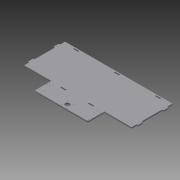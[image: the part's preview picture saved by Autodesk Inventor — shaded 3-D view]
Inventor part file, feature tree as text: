
AUTODESK INVENTOR PART (.ipt)
format: ipt  version: 2013 (Build 170138000, 138)  size: 482,304 bytes
history: native  units: mm
features: reference x12, extrude x10, sketch x10, fillet x1, mirror x1
ambient origin geometry x8: Origin, YZ Plane, XZ Plane, XY Plane, X Axis, Y Axis, Z Axis, Center Point
bodies: Solid1 (feature_tree)
feature tree (34):
  extrude  "Extrusion1"  Depth=81.477mm
  fillet  "Fillet1"  Radius=525.0mm
  extrude  "Extrusion2"  Depth=6.477mm TaperAngle=0.0deg
  extrude  "Extrusion3"  Depth=10.0mm TaperAngle=0.0deg
  extrude  "Extrusion4"  Depth=42.0mm
  extrude  "Extrusion5"  Depth=31.0mm
  mirror  "Mirror2"
  extrude  "Extrusion6"  Depth=10.0mm TaperAngle=0.0deg
  extrude  "Extrusion7"  Depth=25.0mm
  extrude  "Extrusion8"  Depth=6.477mm
  extrude  "Extrusion9"  Depth=2.5mm
  extrude  "Extrusion10"  Depth=1.5mm
  sketch  "Sketch1"  dims[d0=260.0mm d2=81.477mm d3=525.0mm]
  sketch  "Sketch2"  dims[d4=200.0mm d5=6.477mm d6=0.0mm]
  reference  "Reference1"
  reference  "Reference2"
  sketch  "Sketch3"  dims[d7=5.0mm d8=10.0mm d9=0.0mm]
  sketch  "Sketch4"  dims[d10=9.5mm d11=42.0mm]
  sketch  "Sketch5"  dims[d12=22.0mm d13=31.0mm]
  sketch  "Sketch6"  dims[d14=3.0mm d15=10.0mm d16=0.0mm]
  reference  "Reference3"
  reference  "Reference4"
  reference  "Reference5"
  reference  "Reference6"
  reference  "Reference7"
  reference  "Reference8"
  sketch  "Sketch7"  dims[d17=25.0mm d18=25.0mm]
  reference  "Reference9"
  reference  "Reference10"
  sketch  "Sketch8"  dims[d19=25.0mm d20=6.477mm]
  sketch  "Sketch9"  dims[d21=10.0mm d22=0.0mm d23=2.5mm]
  sketch  "Sketch10"  dims[d24=4.0mm d25=1.5mm d27=10.0mm d28=0.0mm d29=4.0mm d30=0.0mm d31=4.0mm d32=0.0mm d33=2.5mm d34=1.5mm d35=4.0mm d36=1.5mm d37=4.0mm d38=2.5mm d39=1.5mm d40=4.0mm d41=1.5mm d42=4.0mm d43=1.5mm d44=4.0mm d45=1.5mm d46=4.0mm d47=1.5mm d48=4.0mm d49=4.0mm d50=0.0mm d51=2.5mm d52=1.5mm d53=4.0mm d54=25.0mm d55=4.0mm d56=0.0mm d57=3.0mm d59=4.0mm d60=4.0mm d61=0.0mm]
  reference  "Reference11"
  reference  "Reference12"
